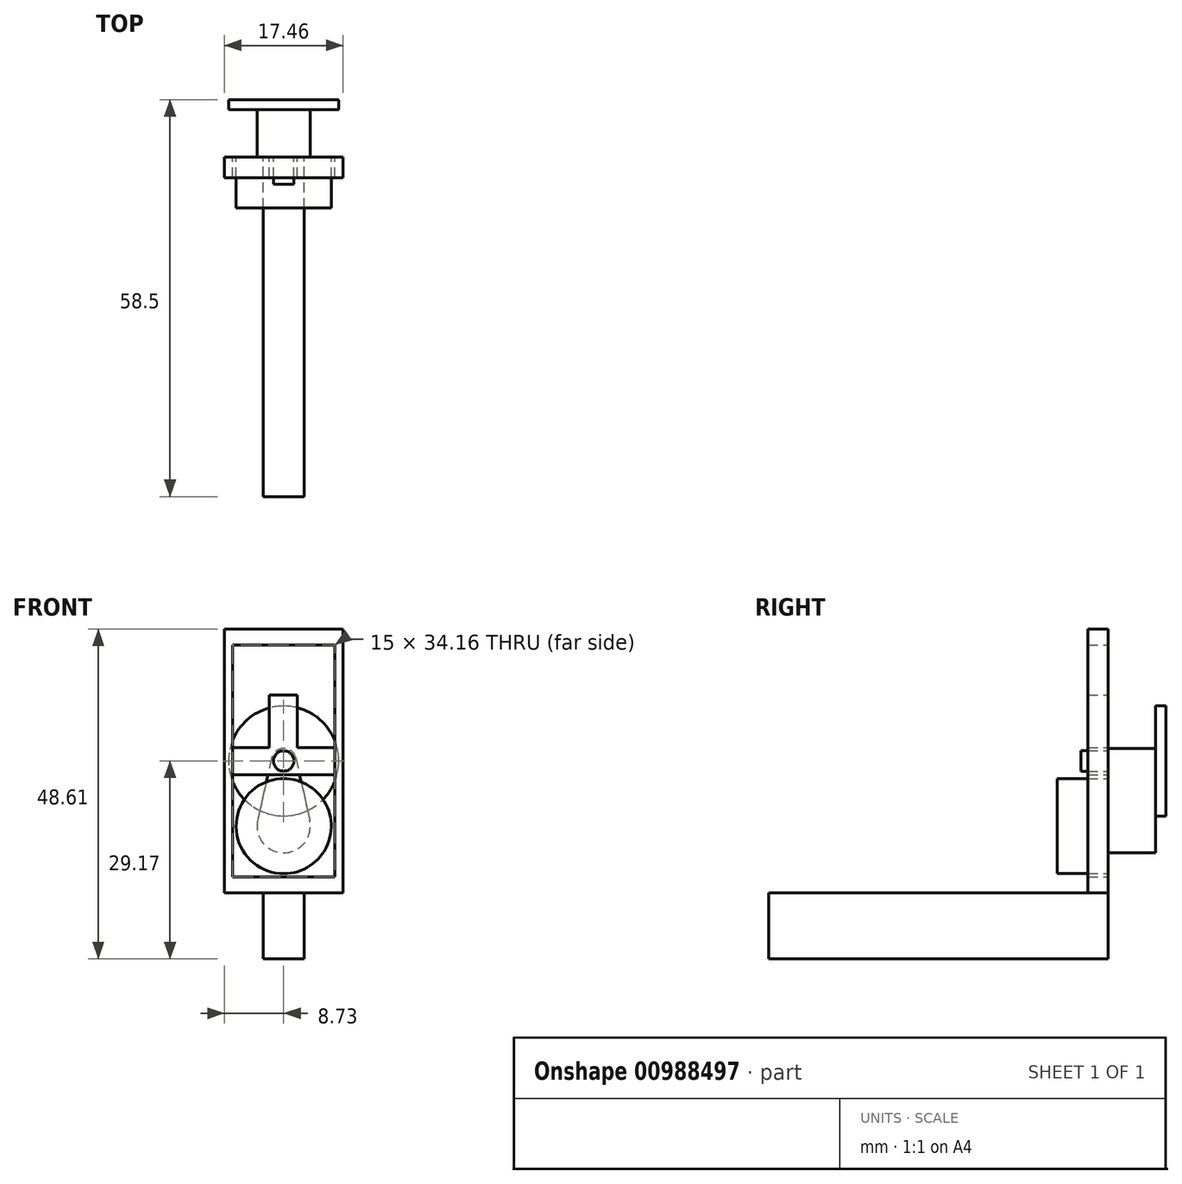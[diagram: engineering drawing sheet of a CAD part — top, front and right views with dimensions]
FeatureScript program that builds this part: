
annotation { "Feature Type Name" : "Feature", "Feature Type Description" : "" }
export const myFeature = defineFeature(function(context is Context, id is Id, definition is map)
    precondition{}
    {
        {
            var Q0;
            Q0=qCreatedBy(makeId("Front.planeOp"),FACE);
            var sketch = newSketch(context, id + "F0", { "sketchPlane" : qUnion([Q0])});
            skArc(sketch, "E0", {"start": v(-5.17, -0.99) * mm, "mid": v(-6, 0) * mm, "end": v(-5.17, 0.99) * mm});
            skLineSegment(sketch, "E1", {"start": v(-0.31, 1.82) * mm, "end": v(-5.17, 0.99) * mm});
            skLineSegment(sketch, "E2", {"start": v(-5.17, -0.99) * mm, "end": v(-0.31, -1.82) * mm});
            skLineSegment(sketch, "E3", {"start": v(0.31, -1.82) * mm, "end": v(5.17, -0.99) * mm});
            skLineSegment(sketch, "E4", {"start": v(5.17, 0.99) * mm, "end": v(0.31, 1.82) * mm});
            skArc(sketch, "E5", {"start": v(-0.31, 1.82) * mm, "mid": v(0, 1.85) * mm, "end": v(0.31, 1.82) * mm});
            skArc(sketch, "E6", {"start": v(5.17, 0.99) * mm, "mid": v(6, 0) * mm, "end": v(5.17, -0.99) * mm});
            skArc(sketch, "E7", {"start": v(-0.31, -1.82) * mm, "mid": v(0, -1.85) * mm, "end": v(0.31, -1.82) * mm});
            skCircle(sketch, "E8", {"center": v(-5, 0) * mm, "radius": 0.5 * mm});
            skCircle(sketch, "E9", {"center": v(5, 0) * mm, "radius": 0.5 * mm});
            skCircle(sketch, "E10", {"center": v(2.95, 0) * mm, "radius": 0.95 * mm});
            skCircle(sketch, "E11", {"center": v(-2.95, 0) * mm, "radius": 0.95 * mm});
            skLineSegment(sketch, "E12", {"start": v(0, 0) * mm, "end": v(0, 2.77) * mm, "construction": true});
            skPoint(sketch, "E12.endSnap0", {"position": v(0, 1.85) * mm});
            skCircle(sketch, "E13", {"center": v(0, 0) * mm, "radius": 1.5 * mm});
            skCircle(sketch, "E14", {"center": v(0, -9.6) * mm, "radius": 7 * mm});
            skSolve(sketch);
        }
        {
            var Q0;
            Q0=qCreatedBy(makeId("Front.planeOp"),FACE);
            var sketch = newSketch(context, id + "F1", { "sketchPlane" : qUnion([Q0])});
            skLineSegment(sketch, "E15", {"start": v(-1.8, 0.4) * mm, "end": v(-3.83, -8.75) * mm});
            skLineSegment(sketch, "E16", {"start": v(1.8, 0.4) * mm, "end": v(3.83, -8.75) * mm});
            skArc(sketch, "E17", {"start": v(-3.83, -8.75) * mm, "mid": v(0, -13.53) * mm, "end": v(3.83, -8.75) * mm});
            skArc(sketch, "E18", {"start": v(-1.8, 0.4) * mm, "mid": v(0, 1.85) * mm, "end": v(1.8, 0.4) * mm});
            skSolve(sketch);
        }
        {
            var Q0;
            Q0=makeQuery(id+"F0.imprint","IMPRINT",FACE,{"disambiguationData":[TD([[makeQuery(id+"F0.imprint","IMPRINT",EDGE,{"derivedFrom":sQuery(id+"F0.wireOp",EDGE,"E14")}),1.0]])]});
            extrude(context, id + "F2", {"entities" : qUnion([Q0]), "depth" : 7.5 * mm, "offsetDistance" : 25 * mm});
        }
        {
            var Q0;
            Q0=makeQuery(id+"F0.imprint","IMPRINT",FACE,{"disambiguationData":[TD([[makeQuery(id+"F0.imprint","IMPRINT",EDGE,{"derivedFrom":sQuery(id+"F0.wireOp",EDGE,"E0")}),-1.0]])]});
            var Q1;
            Q1=makeQuery(id+"F0.imprint","IMPRINT",FACE,{"disambiguationData":[TD([[makeQuery(id+"F0.imprint","IMPRINT",EDGE,{"derivedFrom":sQuery(id+"F0.wireOp",EDGE,"E13")}),1.0]])]});
            extrude(context, id + "F3", {"entities" : qUnion([Q0, Q1]), "oppositeDirection" : true, "depth" : 1 * mm, "offsetDistance" : 25 * mm});
        }
        {
            var Q0;
            Q0=makeQuery(id+"F1.imprint","IMPRINT",FACE,{"disambiguationData":[TD([[makeQuery(id+"F1.imprint","IMPRINT",EDGE,{"derivedFrom":sQuery(id+"F1.wireOp",EDGE,"E15")}),1.0]])]});
            extrude(context, id + "F4", {"entities" : qUnion([Q0]), "operationType" : NewBodyOperationType.ADD, "oppositeDirection" : true, "depth" : 7 * mm, "offsetDistance" : 25 * mm});
        }
        {
            var Q0;
            Q0=makeQuery(id+"F4.opExtrude","CAP_FACE",FACE,{"disambiguationData":[OSD([sQuery(id+"F1.wireOp",EDGE,"E15"),sQuery(id+"F1.wireOp",EDGE,"E16"),sQuery(id+"F1.wireOp",EDGE,"E17"),sQuery(id+"F1.wireOp",EDGE,"E18")])],"isStart":false});
            var sketch = newSketch(context, id + "F5", { "sketchPlane" : qUnion([Q0])});
            skCircle(sketch, "E19", {"center": v(0, 0) * mm, "radius": 8.1 * mm});
            skCircle(sketch, "E20", {"center": v(0, -9.6) * mm, "radius": 1.5 * mm});
            skSolve(sketch);
        }
        {
            var Q0;
            {var subQ0=makeQuery(id+"F4.opExtrude","CAP_EDGE",EDGE,{"disambiguationData":[OSD([sQuery(id+"F1.wireOp",EDGE,"E18")])],"isStart":false});Q0=makeQuery(id+"F5.imprint","IMPRINT",FACE,{"disambiguationData":[TD([[makeQuery(id+"F5.imprint","IMPRINT",EDGE,{"derivedFrom":subQ0}),1.0]])]});}
            var Q1;
            {var subQ5=makeQuery(id+"F4.opExtrude","CAP_EDGE",EDGE,{"disambiguationData":[OSD([sQuery(id+"F1.wireOp",EDGE,"E18")])],"isStart":false});Q1=makeQuery(id+"F5.imprint","IMPRINT",FACE,{"disambiguationData":[TD([[makeQuery(id+"F5.imprint","IMPRINT",EDGE,{"derivedFrom":subQ5}),-1.0]])]});}
            extrude(context, id + "F6", {"entities" : qUnion([Q0, Q1]), "operationType" : NewBodyOperationType.ADD, "depth" : 1.5 * mm, "offsetDistance" : 25 * mm});
        }
        {
            var Q0;
            Q0=makeQuery(id+"F0.imprint","IMPRINT",FACE,{"disambiguationData":[TD([[makeQuery(id+"F0.imprint","IMPRINT",EDGE,{"derivedFrom":sQuery(id+"F0.wireOp",EDGE,"E13")}),1.0]])]});
            extrude(context, id + "F7", {"entities" : qUnion([Q0]), "operationType" : NewBodyOperationType.ADD, "depth" : 4 * mm, "offsetDistance" : 25 * mm});
        }
        {
            var Q0;
            Q0=qCreatedBy(makeId("Front.planeOp"),FACE);
            var sketch = newSketch(context, id + "F8", { "sketchPlane" : qUnion([Q0])});
            skLineSegment(sketch, "E21.top", {"start": v(7.5, -2) * mm, "end": v(-7.5, -2) * mm});
            skLineSegment(sketch, "E21.left", {"start": v(7.5, 2) * mm, "end": v(7.5, -2) * mm});
            skLineSegment(sketch, "E21.right", {"start": v(-7.5, 2) * mm, "end": v(-7.5, -2) * mm});
            skPoint(sketch, "E21.middle", {"position": v(0, 0) * mm});
            skLineSegment(sketch, "E22.bottom", {"start": v(7.5, 17.08) * mm, "end": v(-7.5, 17.08) * mm});
            skLineSegment(sketch, "E22.top", {"start": v(7.5, -17.08) * mm, "end": v(-7.5, -17.08) * mm});
            skLineSegment(sketch, "E22.left", {"start": v(7.5, 17.08) * mm, "end": v(7.5, -17.08) * mm});
            skLineSegment(sketch, "E22.right", {"start": v(-7.5, 17.08) * mm, "end": v(-7.5, -17.08) * mm});
            skLineSegment(sketch, "E23.bottom", {"start": v(8.73, 19.44) * mm, "end": v(-8.73, 19.44) * mm});
            skLineSegment(sketch, "E23.top", {"start": v(8.73, -19.44) * mm, "end": v(-8.73, -19.44) * mm});
            skLineSegment(sketch, "E23.left", {"start": v(8.73, 19.44) * mm, "end": v(8.73, -19.44) * mm});
            skLineSegment(sketch, "E23.right", {"start": v(-8.73, 19.44) * mm, "end": v(-8.73, -19.44) * mm});
            skLineSegment(sketch, "E24.bottom", {"start": v(3, -19.44) * mm, "end": v(-3, -19.44) * mm});
            skLineSegment(sketch, "E24.top", {"start": v(3, -29.17) * mm, "end": v(-3, -29.17) * mm});
            skLineSegment(sketch, "E24.left", {"start": v(3, -19.44) * mm, "end": v(3, -29.17) * mm});
            skLineSegment(sketch, "E24.right", {"start": v(-3, -19.44) * mm, "end": v(-3, -29.17) * mm});
            skPoint(sketch, "E24.middle", {"position": v(0, -24.3) * mm});
            skLineSegment(sketch, "E25", {"start": v(-7.5, 2) * mm, "end": v(-2.13, 2) * mm});
            skLineSegment(sketch, "E26", {"start": v(-2.13, 2) * mm, "end": v(-2.13, 9.68) * mm});
            skLineSegment(sketch, "E27", {"start": v(-2.13, 9.68) * mm, "end": v(2.02, 9.68) * mm});
            skLineSegment(sketch, "E28", {"start": v(2.02, 9.68) * mm, "end": v(2.02, 2) * mm});
            skLineSegment(sketch, "E29", {"start": v(2.02, 2) * mm, "end": v(7.5, 2) * mm});
            skSolve(sketch);
        }
        {
            var Q0;
            {var subQ9=sQuery(id+"F8.wireOp",EDGE,"E21.left");Q0=makeQuery(id+"F8.imprint","IMPRINT",FACE,{"disambiguationData":[TD([[makeQuery(id+"F8.imprint","IMPRINT",EDGE,{"derivedFrom":subQ9}),1.0]])]});}
            extrude(context, id + "F9", {"entities" : qUnion([Q0]), "depth" : 3 * mm, "offsetDistance" : 25 * mm});
        }
        {
            var Q0;
            Q0=makeQuery(id+"F8.imprint","IMPRINT",FACE,{"disambiguationData":[TD([[makeQuery(id+"F8.imprint","IMPRINT",EDGE,{"derivedFrom":sQuery(id+"F8.wireOp",EDGE,"E21.top")}),-1.0]])]});
            extrude(context, id + "F10", {"entities" : qUnion([Q0]), "depth" : 3 * mm, "offsetDistance" : 25 * mm});
        }
        {
            var Q0;
            Q0=makeQuery(id+"F8.imprint","IMPRINT",FACE,{"disambiguationData":[TD([[makeQuery(id+"F8.imprint","IMPRINT",EDGE,{"derivedFrom":sQuery(id+"F8.wireOp",EDGE,"E24.top")}),-1.0]])]});
            extrude(context, id + "F11", {"entities" : qUnion([Q0]), "depth" : 50 * mm, "offsetDistance" : 25 * mm});
        }
    });
